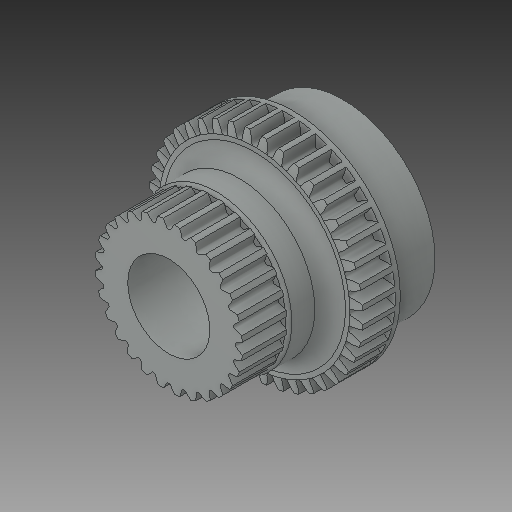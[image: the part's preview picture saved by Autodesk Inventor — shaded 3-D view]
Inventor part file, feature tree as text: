
AUTODESK INVENTOR PART (.ipt)
format: ipt  version: 2017 (Build 210142000, 142)  size: 1,138,176 bytes
history: native  units: in
note: dims shown in document units (in); Inventor stores cm internally (conversion verified against a paired STEP export)
features: fillet x1
ambient origin geometry x8: Origin, YZ Plane, XZ Plane, XY Plane, X Axis, Y Axis, Z Axis, Center Point
bodies: Solid1 (feature_tree)
feature tree (1):
  fillet  "Fillet5"  [1 undecoded]
note: 1 required parameter value undecoded (feature->parameter linkage not recoverable at this tier; creation-order binding heuristic only, values carry confidence <= 0.55)
